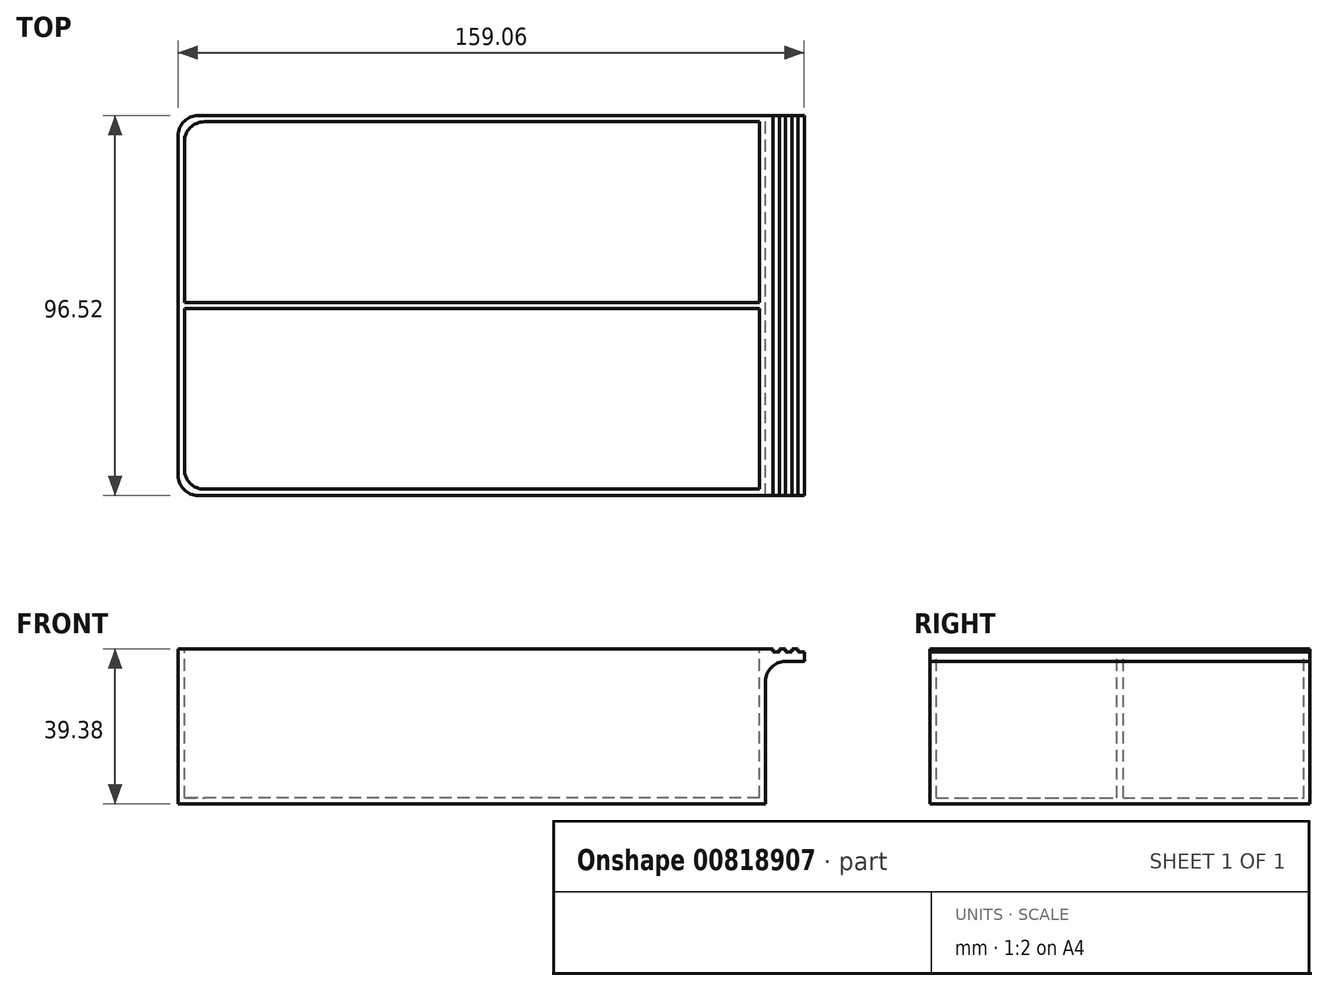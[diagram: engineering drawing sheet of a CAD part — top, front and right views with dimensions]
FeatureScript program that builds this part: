
annotation { "Feature Type Name" : "Feature", "Feature Type Description" : "" }
export const myFeature = defineFeature(function(context is Context, id is Id, definition is map)
    precondition{}
    {
        {
            var Q0;
            Q0=qCreatedBy(makeId("Front.planeOp"),FACE);
            var sketch = newSketch(context, id + "F0", { "sketchPlane" : qUnion([Q0])});
            skLineSegment(sketch, "E0.bottom", {"start": v(74.61, -19.68) * mm, "end": v(-74.61, -19.69) * mm});
            skLineSegment(sketch, "E0.top", {"start": v(74.61, 19.69) * mm, "end": v(-74.61, 19.68) * mm});
            skLineSegment(sketch, "E0.left", {"start": v(74.61, -19.68) * mm, "end": v(74.61, 19.69) * mm});
            skLineSegment(sketch, "E0.right", {"start": v(-74.61, -19.69) * mm, "end": v(-74.61, 19.69) * mm});
            skPoint(sketch, "E0.middle", {"position": v(0, 0) * mm});
            skLineSegment(sketch, "E1.0", {"start": v(-73.03, -18.1) * mm, "end": v(-73.03, 19.69) * mm});
            skLineSegment(sketch, "E2.0", {"start": v(73.03, -18.1) * mm, "end": v(-73.03, -18.1) * mm});
            skLineSegment(sketch, "E3.0", {"start": v(73.03, -18.1) * mm, "end": v(73.03, 19.69) * mm});
            skLineSegment(sketch, "E4.bottom", {"start": v(74.61, 19.69) * mm, "end": v(76.52, 19.69) * mm});
            skLineSegment(sketch, "E4.top", {"start": v(74.61, 16.51) * mm, "end": v(84.45, 16.51) * mm});
            skLineSegment(sketch, "E4.left", {"start": v(74.61, 19.69) * mm, "end": v(74.61, 16.51) * mm});
            skLineSegment(sketch, "E4.right", {"start": v(84.45, 18.9) * mm, "end": v(84.45, 16.51) * mm});
            skLineSegment(sketch, "E5.0", {"start": v(81.28, 19.69) * mm, "end": v(81.28, 18.9) * mm});
            skLineSegment(sketch, "E6.0", {"start": v(79.7, 19.69) * mm, "end": v(79.7, 18.9) * mm});
            skLineSegment(sketch, "E7.0", {"start": v(78.1, 19.69) * mm, "end": v(78.1, 18.9) * mm});
            skLineSegment(sketch, "E8.0", {"start": v(76.52, 19.69) * mm, "end": v(76.52, 18.9) * mm});
            skLineSegment(sketch, "E9.0", {"start": v(76.52, 18.9) * mm, "end": v(78.1, 18.9) * mm});
            skLineSegment(sketch, "E10.0", {"start": v(82.87, 19.69) * mm, "end": v(82.87, 18.9) * mm});
            skLineSegment(sketch, "E11.trimOffspring", {"start": v(81.28, 19.69) * mm, "end": v(82.87, 19.69) * mm});
            skLineSegment(sketch, "E12.trimOffspring", {"start": v(78.1, 19.69) * mm, "end": v(79.7, 19.69) * mm});
            skLineSegment(sketch, "E13.trimOffspring", {"start": v(82.87, 18.9) * mm, "end": v(84.45, 18.9) * mm});
            skLineSegment(sketch, "E14.trimOffspring", {"start": v(79.7, 18.9) * mm, "end": v(81.28, 18.9) * mm});
            skSolve(sketch);
        }
        {
            var Q0;
            Q0 = qSketchRegion(id + "F0", true);
            extrude(context, id + "F1", {"entities" : qUnion([Q0]), "endBound" : BoundingType.SYMMETRIC, "depth" : 96.52 * mm, "offsetDistance" : 25.4 * mm});
        }
        {
            var Q0;
            Q0=makeQuery(id+"F1.opExtrude","SWEPT_FACE",FACE,{"disambiguationData":[OSD([sQuery(id+"F0.wireOp",EDGE,"E0.top"),sQuery(id+"F0.wireOp",EDGE,"E4.bottom")])]});
            shell(context, id + "F2", {"entities" : qUnion([Q0]), "thickness" : 1.59 * mm});
        }
        {
            var Q0;
            {var subQ0=sQuery(id+"F0.wireOp",EDGE,"E0.right");Q0=makeQuery(id+"F2.opShell","OFFSET_EDGE",EDGE,{"disambiguationData":[OSD([subQ0]),TDD([makeQuery(id+"F1.opExtrude","CAP_EDGE",EDGE,{"disambiguationData":[OSD([subQ0])],"isStart":true})])]});}
            var Q1;
            {var subQ0=sQuery(id+"F0.wireOp",EDGE,"E0.right");Q1=makeQuery(id+"F2.opShell","OFFSET_EDGE",EDGE,{"disambiguationData":[OSD([subQ0]),TDD([makeQuery(id+"F1.opExtrude","CAP_EDGE",EDGE,{"disambiguationData":[OSD([subQ0])],"isStart":false})])]});}
            var Q2;
            Q2=makeQuery(id+"F1.opExtrude","CAP_EDGE",EDGE,{"disambiguationData":[OSD([sQuery(id+"F0.wireOp",EDGE,"E0.right")])],"isStart":false});
            var Q3;
            Q3=makeQuery(id+"F1.opExtrude","CAP_EDGE",EDGE,{"disambiguationData":[OSD([sQuery(id+"F0.wireOp",EDGE,"E0.right")])],"isStart":true});
            fillet(context, id + "F3", {"entities" : qUnion([Q0, Q1, Q2, Q3]), "radius" : 5.08 * mm, "tangentPropagation" : true, "allowEdgeOverflow" : false});
        }
        {
            var Q0;
            Q0=makeQuery(id+"F2.opShell","OFFSET_FACE",FACE,{"disambiguationData":[OSD([sQuery(id+"F0.wireOp",EDGE,"E4.top")])]});
            extrude(context, id + "F4", {"entities" : qUnion([Q0]), "operationType" : NewBodyOperationType.ADD, "depth" : 1.59 * mm, "offsetDistance" : 25.4 * mm});
        }
        {
            var Q0;
            {var subQ0=sQuery(id+"F0.wireOp",EDGE,"E1.0");Q0=makeQuery(id+"F0.imprint","IMPRINT",FACE,{"disambiguationData":[TD([[makeQuery(id+"F0.imprint","IMPRINT",EDGE,{"derivedFrom":subQ0}),-1.0]])]});}
            extrude(context, id + "F5", {"entities" : qUnion([Q0]), "operationType" : NewBodyOperationType.ADD, "endBound" : BoundingType.SYMMETRIC, "depth" : 1.59 * mm, "offsetDistance" : 25.4 * mm});
        }
        {
            var Q0;
            Q0=makeQuery(id+"F1.opExtrude","SWEPT_EDGE",EDGE,{"disambiguationData":[OSD([sQuery(id+"F0.wireOp",EDGE,"E0.left"),sQuery(id+"F0.wireOp",EDGE,"E4.top"),sQuery(id+"F0.wireOp",EDGE,"E4.left")])]});
            fillet(context, id + "F6", {"entities" : qUnion([Q0]), "radius" : 5.08 * mm, "tangentPropagation" : true, "allowEdgeOverflow" : false});
        }
    });
